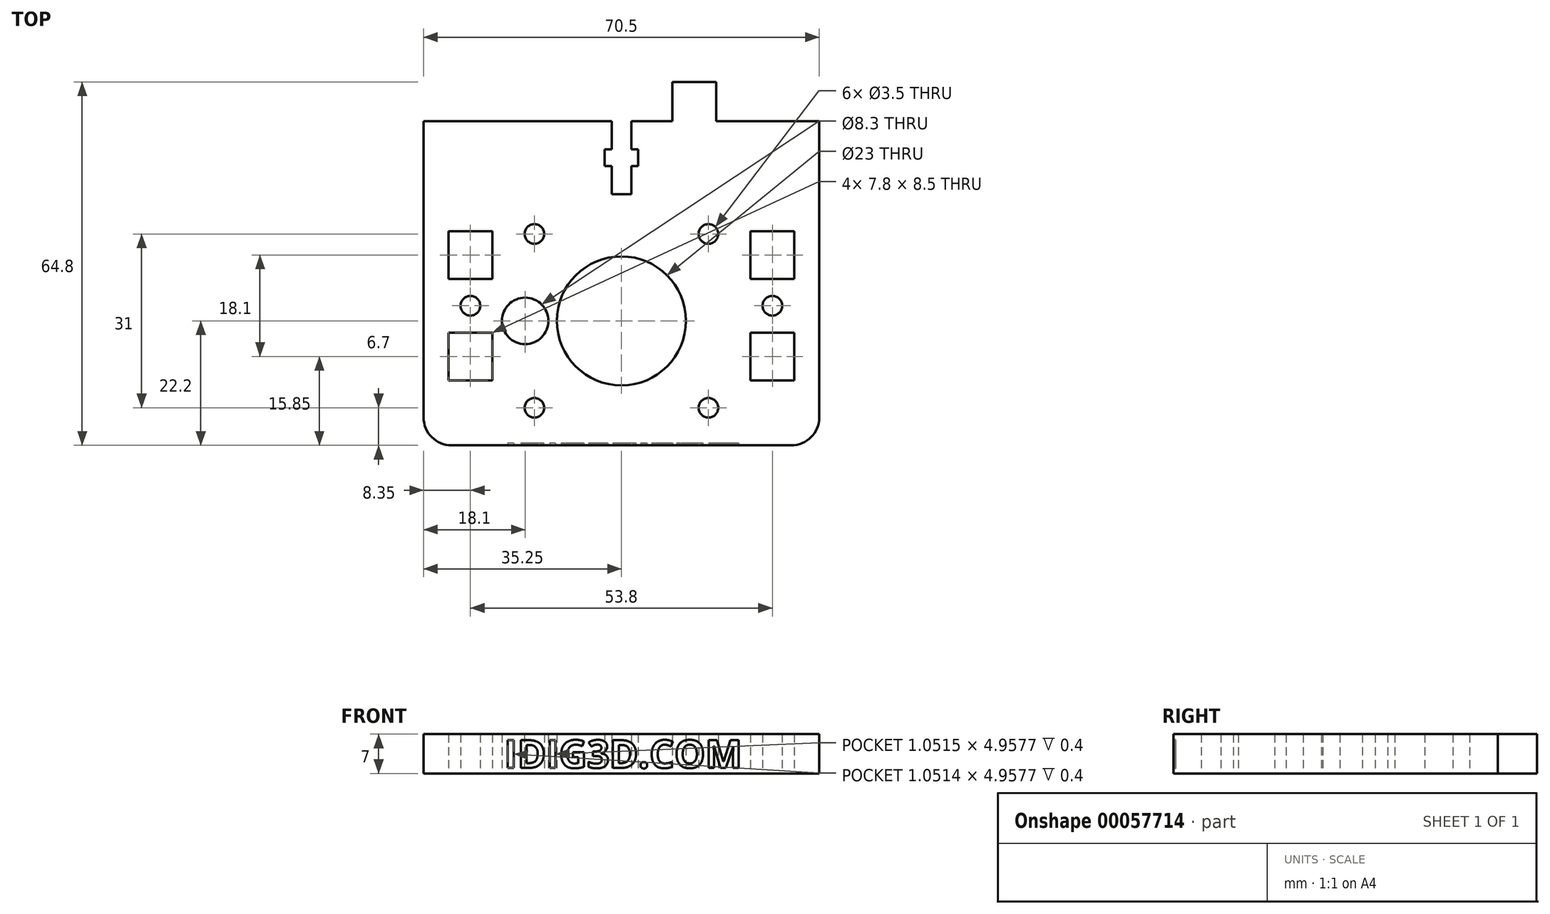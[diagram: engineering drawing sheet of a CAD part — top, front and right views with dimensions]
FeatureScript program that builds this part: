
annotation { "Feature Type Name" : "Feature", "Feature Type Description" : "" }
export const myFeature = defineFeature(function(context is Context, id is Id, definition is map)
    precondition{}
    {
        {
            var Q0;
            Q0=qCreatedBy(makeId("Top.planeOp"),FACE);
            var sketch = newSketch(context, id + "F0", { "sketchPlane" : qUnion([Q0])});
            skLineSegment(sketch, "E0.rect.bottom", {"start": v(-35.25, 28.9) * mm, "end": v(35.25, 28.9) * mm});
            skLineSegment(sketch, "E0.rect.top", {"start": v(-30.25, -28.9) * mm, "end": v(30.25, -28.9) * mm});
            skLineSegment(sketch, "E0.rect.left", {"start": v(-35.25, 28.9) * mm, "end": v(-35.25, -23.9) * mm});
            skLineSegment(sketch, "E0.rect.right", {"start": v(35.25, 28.9) * mm, "end": v(35.25, -23.9) * mm});
            skPoint(sketch, "E0.rect.middle", {"position": v(0, 0) * mm});
            skCircle(sketch, "E1", {"center": v(0, -6.7) * mm, "radius": 11.5 * mm});
            skLineSegment(sketch, "E2.rect.bottom", {"start": v(-15.5, 8.8) * mm, "end": v(15.5, 8.8) * mm, "construction": true});
            skLineSegment(sketch, "E2.rect.top", {"start": v(-15.5, -22.2) * mm, "end": v(15.5, -22.2) * mm, "construction": true});
            skLineSegment(sketch, "E2.rect.left", {"start": v(-15.5, 8.8) * mm, "end": v(-15.5, -22.2) * mm, "construction": true});
            skLineSegment(sketch, "E2.rect.right", {"start": v(15.5, 8.8) * mm, "end": v(15.5, -22.2) * mm, "construction": true});
            skCircle(sketch, "E3", {"center": v(-15.5, 8.8) * mm, "radius": 1.75 * mm});
            skCircle(sketch, "E4", {"center": v(15.5, 8.8) * mm, "radius": 1.75 * mm});
            skCircle(sketch, "E5", {"center": v(15.5, -22.2) * mm, "radius": 1.75 * mm});
            skCircle(sketch, "E6", {"center": v(-15.5, -22.2) * mm, "radius": 1.75 * mm});
            skCircle(sketch, "E7", {"center": v(-17.15, -6.7) * mm, "radius": 4.15 * mm});
            skLineSegment(sketch, "E8.rect.bottom", {"start": v(-23, 0.8) * mm, "end": v(-30.8, 0.8) * mm});
            skLineSegment(sketch, "E8.rect.top", {"start": v(-23, 9.3) * mm, "end": v(-30.8, 9.3) * mm});
            skLineSegment(sketch, "E8.rect.left", {"start": v(-23, 0.8) * mm, "end": v(-23, 9.3) * mm});
            skLineSegment(sketch, "E8.rect.right", {"start": v(-30.8, 0.8) * mm, "end": v(-30.8, 9.3) * mm});
            skPoint(sketch, "E8.rect.middle", {"position": v(-26.9, 5.05) * mm});
            skCircle(sketch, "E9", {"center": v(-26.9, -4) * mm, "radius": 1.75 * mm});
            skLineSegment(sketch, "E10", {"start": v(-26.9, -4) * mm, "end": v(-5.82, -4) * mm, "construction": true});
            skLineSegment(sketch, "E11", {"start": v(0, -14.58) * mm, "end": v(0, -6.7) * mm, "construction": true});
            skLineSegment(sketch, "E12.MirrorCS", {"start": v(-23, -8.8) * mm, "end": v(-23, -17.3) * mm});
            skLineSegment(sketch, "E13.MirrorCS", {"start": v(-30.8, -8.8) * mm, "end": v(-30.8, -17.3) * mm});
            skPoint(sketch, "E14.MirrorP", {"position": v(-26.9, -13.05) * mm});
            skLineSegment(sketch, "E15.MirrorCS", {"start": v(-23, -17.3) * mm, "end": v(-30.8, -17.3) * mm});
            skLineSegment(sketch, "E16.MirrorCS", {"start": v(-23, -8.8) * mm, "end": v(-30.8, -8.8) * mm});
            skLineSegment(sketch, "E17.MirrorCS", {"start": v(23, 0.8) * mm, "end": v(23, 9.3) * mm});
            skCircle(sketch, "E18.MirrorC", {"center": v(26.9, -4) * mm, "radius": 1.75 * mm});
            skLineSegment(sketch, "E19.MirrorCS", {"start": v(30.8, -8.8) * mm, "end": v(30.8, -17.3) * mm});
            skLineSegment(sketch, "E20.MirrorCS", {"start": v(23, -17.3) * mm, "end": v(30.8, -17.3) * mm});
            skPoint(sketch, "E21.MirrorP", {"position": v(26.9, -13.05) * mm});
            skLineSegment(sketch, "E22.MirrorCS", {"start": v(23, -8.8) * mm, "end": v(30.8, -8.8) * mm});
            skPoint(sketch, "E23.MirrorP", {"position": v(26.9, 5.05) * mm});
            skLineSegment(sketch, "E24.MirrorCS", {"start": v(23, -8.8) * mm, "end": v(23, -17.3) * mm});
            skLineSegment(sketch, "E25.MirrorCS", {"start": v(26.9, -4) * mm, "end": v(5.82, -4) * mm, "construction": true});
            skLineSegment(sketch, "E26.MirrorCS", {"start": v(23, 0.8) * mm, "end": v(30.8, 0.8) * mm});
            skLineSegment(sketch, "E27.MirrorCS", {"start": v(30.8, 0.8) * mm, "end": v(30.8, 9.3) * mm});
            skLineSegment(sketch, "E28.MirrorCS", {"start": v(23, 9.3) * mm, "end": v(30.8, 9.3) * mm});
            skPoint(sketch, "E29.visualSharp", {"position": v(-35.25, -28.9) * mm});
            skArc(sketch, "E29.filletArc", {"start": v(-35.25, -23.9) * mm, "mid": v(-33.79, -27.44) * mm, "end": v(-30.25, -28.9) * mm});
            skPoint(sketch, "E30.visualSharp", {"position": v(35.25, -28.9) * mm});
            skArc(sketch, "E30.filletArc", {"start": v(30.25, -28.9) * mm, "mid": v(33.79, -27.44) * mm, "end": v(35.25, -23.9) * mm});
            skLineSegment(sketch, "E31.rect.bottom", {"start": v(1.75, 28.9) * mm, "end": v(-1.75, 28.9) * mm});
            skLineSegment(sketch, "E31.rect.top", {"start": v(1.75, 15.9) * mm, "end": v(-1.75, 15.9) * mm});
            skLineSegment(sketch, "E31.rect.left", {"start": v(1.75, 28.9) * mm, "end": v(1.75, 15.9) * mm});
            skLineSegment(sketch, "E31.rect.right", {"start": v(-1.75, 28.9) * mm, "end": v(-1.75, 15.9) * mm});
            skPoint(sketch, "E31.rect.middle", {"position": v(0, 22.4) * mm});
            skLineSegment(sketch, "E32.rect.bottom", {"start": v(3, 23.9) * mm, "end": v(-3, 23.9) * mm});
            skLineSegment(sketch, "E32.rect.top", {"start": v(3, 20.9) * mm, "end": v(-3, 20.9) * mm});
            skLineSegment(sketch, "E32.rect.left", {"start": v(3, 23.9) * mm, "end": v(3, 20.9) * mm});
            skLineSegment(sketch, "E32.rect.right", {"start": v(-3, 23.9) * mm, "end": v(-3, 20.9) * mm});
            skPoint(sketch, "E32.rect.middle.positionSnap0", {"position": v(0, 15.9) * mm});
            skPoint(sketch, "E32.rect.centerSnap0", {"position": v(0, 15.9) * mm});
            skLineSegment(sketch, "E33.bottom", {"start": v(-16.9, 28.9) * mm, "end": v(-9.1, 28.9) * mm});
            skLineSegment(sketch, "E33.top", {"start": v(-16.9, 35.9) * mm, "end": v(-9.1, 35.9) * mm});
            skLineSegment(sketch, "E33.left", {"start": v(-16.9, 28.9) * mm, "end": v(-16.9, 35.9) * mm});
            skLineSegment(sketch, "E33.right", {"start": v(-9.1, 28.9) * mm, "end": v(-9.1, 35.9) * mm});
            skLineSegment(sketch, "E34.MirrorCS", {"start": v(16.9, 28.9) * mm, "end": v(16.9, 35.9) * mm});
            skLineSegment(sketch, "E35.MirrorCS", {"start": v(16.9, 35.9) * mm, "end": v(9.1, 35.9) * mm});
            skLineSegment(sketch, "E36.MirrorCS", {"start": v(16.9, 28.9) * mm, "end": v(9.1, 28.9) * mm});
            skLineSegment(sketch, "E37.MirrorCS", {"start": v(9.1, 28.9) * mm, "end": v(9.1, 35.9) * mm});
            skSolve(sketch);
        }
        {
            var Q0;
            Q0=makeQuery(id+"F0.imprint","IMPRINT",FACE,{"disambiguationData":[TD([[makeQuery(id+"F0.imprint","IMPRINT",EDGE,{"derivedFrom":sQuery(id+"F0.wireOp",EDGE,"E33.bottom")}),1.0]])]});
            var Q1;
            Q1=makeQuery(id+"F0.imprint","IMPRINT",FACE,{"disambiguationData":[TD([[makeQuery(id+"F0.imprint","IMPRINT",EDGE,{"derivedFrom":sQuery(id+"F0.wireOp",EDGE,"E34.MirrorCS")}),1.0]])]});
            var Q2;
            Q2=makeQuery(id+"F0.imprint","IMPRINT",FACE,{"disambiguationData":[TD([[makeQuery(id+"F0.imprint","IMPRINT",EDGE,{"derivedFrom":sQuery(id+"F0.wireOp",EDGE,"E0.rect.top")}),1.0]])]});
            extrude(context, id + "F1", {"entities" : qUnion([Q0, Q1, Q2]), "depth" : 7 * mm});
        }
        {
            var Q0;
            Q0=makeQuery(id+"F1.opExtrude","SWEPT_FACE",FACE,{"disambiguationData":[OSD([sQuery(id+"F0.wireOp",EDGE,"E0.rect.top")])]});
            var sketch = newSketch(context, id + "F2", { "sketchPlane" : qUnion([Q0])});
            skText(sketch, "E38", { "text": "IDIG3D.COM", "fontName": "OpenSans-Bold.ttf"});
            skPoint(sketch, "E39.0", {"position": v(0, 0) * mm});
            const initialGuessF2  = {"E38": [-0.02086, 0.00097, 1, 0, 0.005]};
            skSetInitialGuess(sketch, initialGuessF2);
            skSolve(sketch);
        }
        {
            var Q0;
            Q0 = qSketchRegion(id + "F2", true);
            extrude(context, id + "F3", {"entities" : qUnion([Q0]), "operationType" : NewBodyOperationType.REMOVE, "oppositeDirection" : true, "depth" : .4 * mm});
        }
    });
